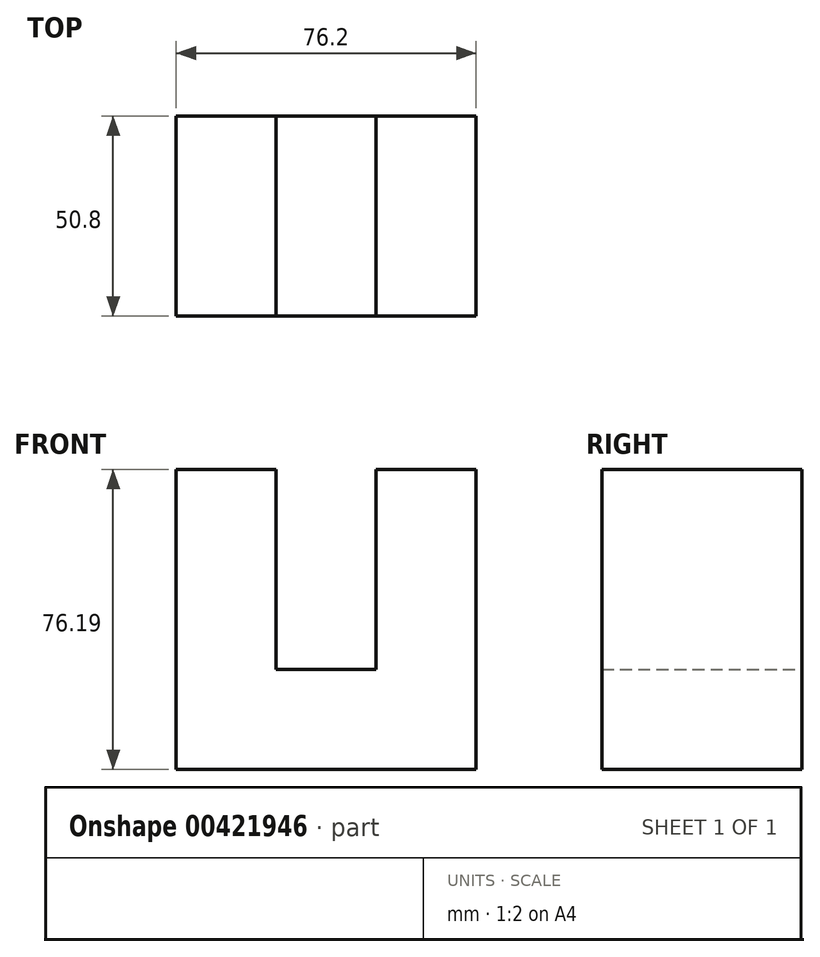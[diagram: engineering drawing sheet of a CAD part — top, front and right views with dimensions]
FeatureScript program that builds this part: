
annotation { "Feature Type Name" : "Feature", "Feature Type Description" : "" }
export const myFeature = defineFeature(function(context is Context, id is Id, definition is map)
    precondition{}
    {
        {
            var Q0;
            Q0=qCreatedBy(makeId("Front.planeOp"),FACE);
            var sketch = newSketch(context, id + "F0", { "sketchPlane" : qUnion([Q0])});
            skLineSegment(sketch, "E0", {"start": v(-76.2, 0) * mm, "end": v(0, 0) * mm});
            skLineSegment(sketch, "E1", {"start": v(-76.2, 0) * mm, "end": v(-76.2, 76.2) * mm});
            skLineSegment(sketch, "E2", {"start": v(0, 0) * mm, "end": v(0, 76.2) * mm});
            skLineSegment(sketch, "E3", {"start": v(-76.2, 76.2) * mm, "end": v(-50.8, 76.2) * mm});
            skLineSegment(sketch, "E4", {"start": v(0, 76.2) * mm, "end": v(-25.4, 76.2) * mm});
            skLineSegment(sketch, "E5", {"start": v(-50.8, 76.2) * mm, "end": v(-50.8, 25.4) * mm});
            skLineSegment(sketch, "E6", {"start": v(-25.4, 76.2) * mm, "end": v(-25.4, 25.4) * mm});
            skLineSegment(sketch, "E7", {"start": v(-50.8, 25.4) * mm, "end": v(-25.4, 25.4) * mm});
            skSolve(sketch);
        }
        {
            var Q0;
            Q0=makeQuery(id+"F0.imprint","IMPRINT",FACE,{"disambiguationData":[TD([[makeQuery(id+"F0.imprint","IMPRINT",EDGE,{"derivedFrom":sQuery(id+"F0.wireOp",EDGE,"E0")}),1.0]])]});
            extrude(context, id + "F1", {"entities" : qUnion([Q0]), "depth" : 50.8 * mm});
        }
    });
